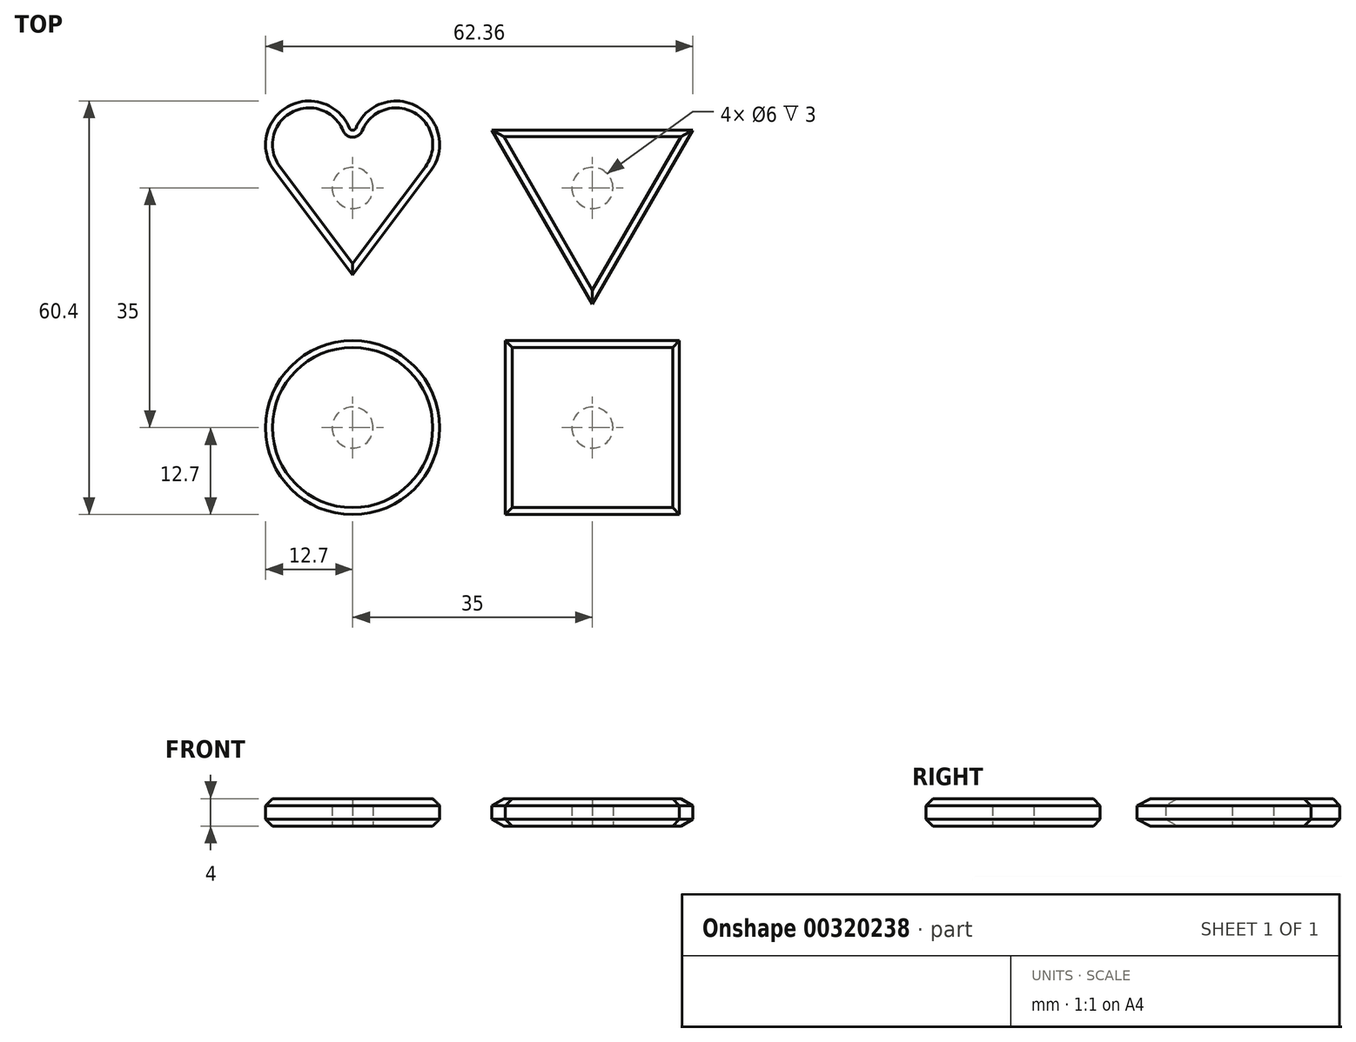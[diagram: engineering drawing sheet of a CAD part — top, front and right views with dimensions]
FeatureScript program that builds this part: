
annotation { "Feature Type Name" : "Feature", "Feature Type Description" : "" }
export const myFeature = defineFeature(function(context is Context, id is Id, definition is map)
    precondition{}
    {
        {
            var Q0;
            Q0=qCreatedBy(makeId("Top.planeOp"),FACE);
            var sketch = newSketch(context, id + "F0", { "sketchPlane" : qUnion([Q0])});
            skCircle(sketch, "E0", {"center": v(0, 0) * mm, "radius": 3 * mm});
            skLineSegment(sketch, "E1.bottom", {"start": v(12.7, 12.7) * mm, "end": v(-12.7, 12.7) * mm, "construction": true});
            skLineSegment(sketch, "E1.top", {"start": v(12.7, -12.7) * mm, "end": v(-12.7, -12.7) * mm, "construction": true});
            skLineSegment(sketch, "E1.left", {"start": v(12.7, 12.7) * mm, "end": v(12.7, -12.7) * mm, "construction": true});
            skLineSegment(sketch, "E1.right", {"start": v(-12.7, 12.7) * mm, "end": v(-12.7, -12.7) * mm, "construction": true});
            skSolve(sketch);
        }
        {
            var Q0;
            Q0=qCreatedBy(makeId("Top.planeOp"),FACE);
            var sketch = newSketch(context, id + "F1", { "sketchPlane" : qUnion([Q0])});
            skCircle(sketch, "E2", {"center": v(0, 0) * mm, "radius": 12.7 * mm});
            skSolve(sketch);
        }
        {
            var Q0;
            Q0=qCreatedBy(makeId("Top.planeOp"),FACE);
            var sketch = newSketch(context, id + "F2", { "sketchPlane" : qUnion([Q0])});
            skCircle(sketch, "E3.cCircle", {"center": v(0, 0) * mm, "radius": 8.47 * mm, "construction": true});
            skLineSegment(sketch, "E3.0", {"start": v(-14.66, 8.47) * mm, "end": v(14.66, 8.47) * mm});
            skLineSegment(sketch, "E3.1", {"start": v(14.66, 8.47) * mm, "end": v(0, -16.93) * mm});
            skLineSegment(sketch, "E3.2", {"start": v(0, -16.93) * mm, "end": v(-14.66, 8.47) * mm});
            skPoint(sketch, "E3.0.midPoint", {"position": v(0, 8.47) * mm});
            skCircle(sketch, "E4", {"center": v(0, 0) * mm, "radius": 12.7 * mm, "construction": true});
            skLineSegment(sketch, "E5", {"start": v(14.66, 8.47) * mm, "end": v(14.66, -16.93) * mm, "construction": true});
            skSolve(sketch);
        }
        {
            var Q0;
            Q0=qCreatedBy(makeId("Top.planeOp"),FACE);
            var sketch = newSketch(context, id + "F3", { "sketchPlane" : qUnion([Q0])});
            skArc(sketch, "E6", {"start": v(0, 6.35) * mm, "mid": v(-8.36, 12.37) * mm, "end": v(-11.43, 2.54) * mm});
            skArc(sketch, "E7", {"start": v(11.43, 2.54) * mm, "mid": v(8.36, 12.37) * mm, "end": v(0, 6.35) * mm});
            skLineSegment(sketch, "E8", {"start": v(-11.43, 2.54) * mm, "end": v(0, -12.7) * mm});
            skLineSegment(sketch, "E9", {"start": v(0, -12.7) * mm, "end": v(11.43, 2.54) * mm});
            skSolve(sketch);
        }
        {
            var Q0;
            Q0=qCreatedBy(makeId("Top.planeOp"),FACE);
            var sketch = newSketch(context, id + "F4", { "sketchPlane" : qUnion([Q0])});
            skLineSegment(sketch, "E10.bottom", {"start": v(12.7, -12.7) * mm, "end": v(-12.7, -12.7) * mm});
            skLineSegment(sketch, "E10.top", {"start": v(12.7, 12.7) * mm, "end": v(-12.7, 12.7) * mm});
            skLineSegment(sketch, "E10.left", {"start": v(12.7, -12.7) * mm, "end": v(12.7, 12.7) * mm});
            skLineSegment(sketch, "E10.right", {"start": v(-12.7, -12.7) * mm, "end": v(-12.7, 12.7) * mm});
            skPoint(sketch, "E10.middle", {"position": v(0, 0) * mm});
            skSolve(sketch);
        }
        {
            var Q0;
            Q0 = qSketchRegion(id + "F3", true);
            extrude(context, id + "F5", {"entities" : qUnion([Q0]), "depth" : 4 * mm});
        }
        {
            var Q0;
            Q0 = qSketchRegion(id + "F1", true);
            extrude(context, id + "F6", {"entities" : qUnion([Q0]), "depth" : 4 * mm});
        }
        {
            var Q0;
            Q0 = qSketchRegion(id + "F2", true);
            extrude(context, id + "F7", {"entities" : qUnion([Q0]), "depth" : 4 * mm});
        }
        {
            var Q0;
            Q0 = qSketchRegion(id + "F4", true);
            extrude(context, id + "F8", {"entities" : qUnion([Q0]), "depth" : 4 * mm});
        }
        {
            var Q0;
            Q0 = qSketchRegion(id + "F0", true);
            extrude(context, id + "F9", {"entities" : qUnion([Q0]), "operationType" : NewBodyOperationType.REMOVE, "depth" : 3 * mm});
        }
        {
            var Q0;
            Q0=makeQuery(id+"F5.opExtrude","SWEPT_BODY",BODY,{"disambiguationData":[OSD([sQuery(id+"F3.wireOp",EDGE,"E6"),sQuery(id+"F3.wireOp",EDGE,"E7"),sQuery(id+"F3.wireOp",EDGE,"E8"),sQuery(id+"F3.wireOp",EDGE,"E9")])]});
            var Q1;
            Q1=makeQuery(id+"F6.opExtrude","SWEPT_BODY",BODY,{"disambiguationData":[OSD([sQuery(id+"F1.wireOp",EDGE,"E2")])]});
            var Q2;
            Q2=makeQuery(id+"F8.opExtrude","CAP_EDGE",EDGE,{"disambiguationData":[OSD([sQuery(id+"F4.wireOp",EDGE,"E10.bottom")])],"isStart":false});
            var Q3;
            Q3=makeQuery(id+"F8.opExtrude","CAP_EDGE",EDGE,{"disambiguationData":[OSD([sQuery(id+"F4.wireOp",EDGE,"E10.bottom")])],"isStart":false});
            transform(context, id + "F10", {"entities" : qUnion([Q0, Q1]), "transformType" : TransformType.TRANSLATION_DISTANCE, "transformDirection" : qUnion([Q3]), "distance" : 35 * mm, "makeCopy" : false});
        }
        {
            var Q0;
            Q0=makeQuery(id+"F8.opExtrude","SWEPT_BODY",BODY,{"disambiguationData":[OSD([sQuery(id+"F4.wireOp",EDGE,"E10.bottom"),sQuery(id+"F4.wireOp",EDGE,"E10.top"),sQuery(id+"F4.wireOp",EDGE,"E10.left"),sQuery(id+"F4.wireOp",EDGE,"E10.right")])]});
            var Q1;
            Q1=makeQuery(id+"F6.opExtrude","SWEPT_BODY",BODY,{"disambiguationData":[OSD([sQuery(id+"F1.wireOp",EDGE,"E2")])]});
            var Q2;
            Q2=makeQuery(id+"F8.opExtrude","CAP_EDGE",EDGE,{"disambiguationData":[OSD([sQuery(id+"F4.wireOp",EDGE,"E10.left")])],"isStart":false});
            var Q3;
            Q3=makeQuery(id+"F8.opExtrude","CAP_EDGE",EDGE,{"disambiguationData":[OSD([sQuery(id+"F4.wireOp",EDGE,"E10.left")])],"isStart":false});
            transform(context, id + "F11", {"entities" : qUnion([Q0, Q1]), "transformType" : TransformType.TRANSLATION_DISTANCE, "transformDirection" : qUnion([Q3]), "distance" : 35 * mm, "oppositeDirection" : true, "makeCopy" : false});
        }
        {
            var Q0;
            Q0=makeQuery(id+"F5.opExtrude","SWEPT_EDGE",EDGE,{"disambiguationData":[OSD([sQuery(id+"F3.wireOp",EDGE,"E6"),sQuery(id+"F3.wireOp",EDGE,"E7")])]});
            fillet(context, id + "F12", {"entities" : qUnion([Q0]), "radius" : 0.5 * mm, "tangentPropagation" : true, "allowEdgeOverflow" : false});
        }
        {
            var Q0;
            Q0=makeQuery(id+"F7.opExtrude","CAP_EDGE",EDGE,{"disambiguationData":[OSD([sQuery(id+"F2.wireOp",EDGE,"E3.1")])],"isStart":true});
            var Q1;
            Q1=makeQuery(id+"F7.opExtrude","CAP_EDGE",EDGE,{"disambiguationData":[OSD([sQuery(id+"F2.wireOp",EDGE,"E3.0")])],"isStart":true});
            var Q2;
            Q2=makeQuery(id+"F7.opExtrude","CAP_EDGE",EDGE,{"disambiguationData":[OSD([sQuery(id+"F2.wireOp",EDGE,"E3.2")])],"isStart":true});
            var Q3;
            Q3=makeQuery(id+"F5.opExtrude","CAP_EDGE",EDGE,{"disambiguationData":[OSD([sQuery(id+"F3.wireOp",EDGE,"E7")])],"isStart":true});
            var Q4;
            Q4=makeQuery(id+"F8.opExtrude","CAP_EDGE",EDGE,{"disambiguationData":[OSD([sQuery(id+"F4.wireOp",EDGE,"E10.right")])],"isStart":true});
            var Q5;
            Q5=makeQuery(id+"F8.opExtrude","CAP_EDGE",EDGE,{"disambiguationData":[OSD([sQuery(id+"F4.wireOp",EDGE,"E10.top")])],"isStart":true});
            var Q6;
            Q6=makeQuery(id+"F8.opExtrude","CAP_EDGE",EDGE,{"disambiguationData":[OSD([sQuery(id+"F4.wireOp",EDGE,"E10.left")])],"isStart":true});
            var Q7;
            Q7=makeQuery(id+"F8.opExtrude","CAP_EDGE",EDGE,{"disambiguationData":[OSD([sQuery(id+"F4.wireOp",EDGE,"E10.bottom")])],"isStart":true});
            var Q8;
            Q8=makeQuery(id+"F6.opExtrude","CAP_EDGE",EDGE,{"disambiguationData":[OSD([sQuery(id+"F1.wireOp",EDGE,"E2")])],"isStart":true});
            var Q9;
            Q9=makeQuery(id+"F5.opExtrude","CAP_FACE",FACE,{"disambiguationData":[OSD([sQuery(id+"F3.wireOp",EDGE,"E6"),sQuery(id+"F3.wireOp",EDGE,"E7"),sQuery(id+"F3.wireOp",EDGE,"E8"),sQuery(id+"F3.wireOp",EDGE,"E9")])],"isStart":false});
            var Q10;
            Q10=makeQuery(id+"F6.opExtrude","CAP_FACE",FACE,{"disambiguationData":[OSD([sQuery(id+"F1.wireOp",EDGE,"E2")])],"isStart":false});
            var Q11;
            Q11=makeQuery(id+"F8.opExtrude","CAP_FACE",FACE,{"disambiguationData":[OSD([sQuery(id+"F4.wireOp",EDGE,"E10.bottom"),sQuery(id+"F4.wireOp",EDGE,"E10.top"),sQuery(id+"F4.wireOp",EDGE,"E10.left"),sQuery(id+"F4.wireOp",EDGE,"E10.right")])],"isStart":false});
            var Q12;
            Q12=makeQuery(id+"F7.opExtrude","CAP_FACE",FACE,{"disambiguationData":[OSD([sQuery(id+"F2.wireOp",EDGE,"E3.0"),sQuery(id+"F2.wireOp",EDGE,"E3.1"),sQuery(id+"F2.wireOp",EDGE,"E3.2")])],"isStart":false});
            chamfer(context, id + "F13", {"entities" : qUnion([Q0, Q1, Q2, Q3, Q4, Q5, Q6, Q7, Q8, Q9, Q10, Q11, Q12]), "width" : 1 * mm, "tangentPropagation" : true});
        }
    });
